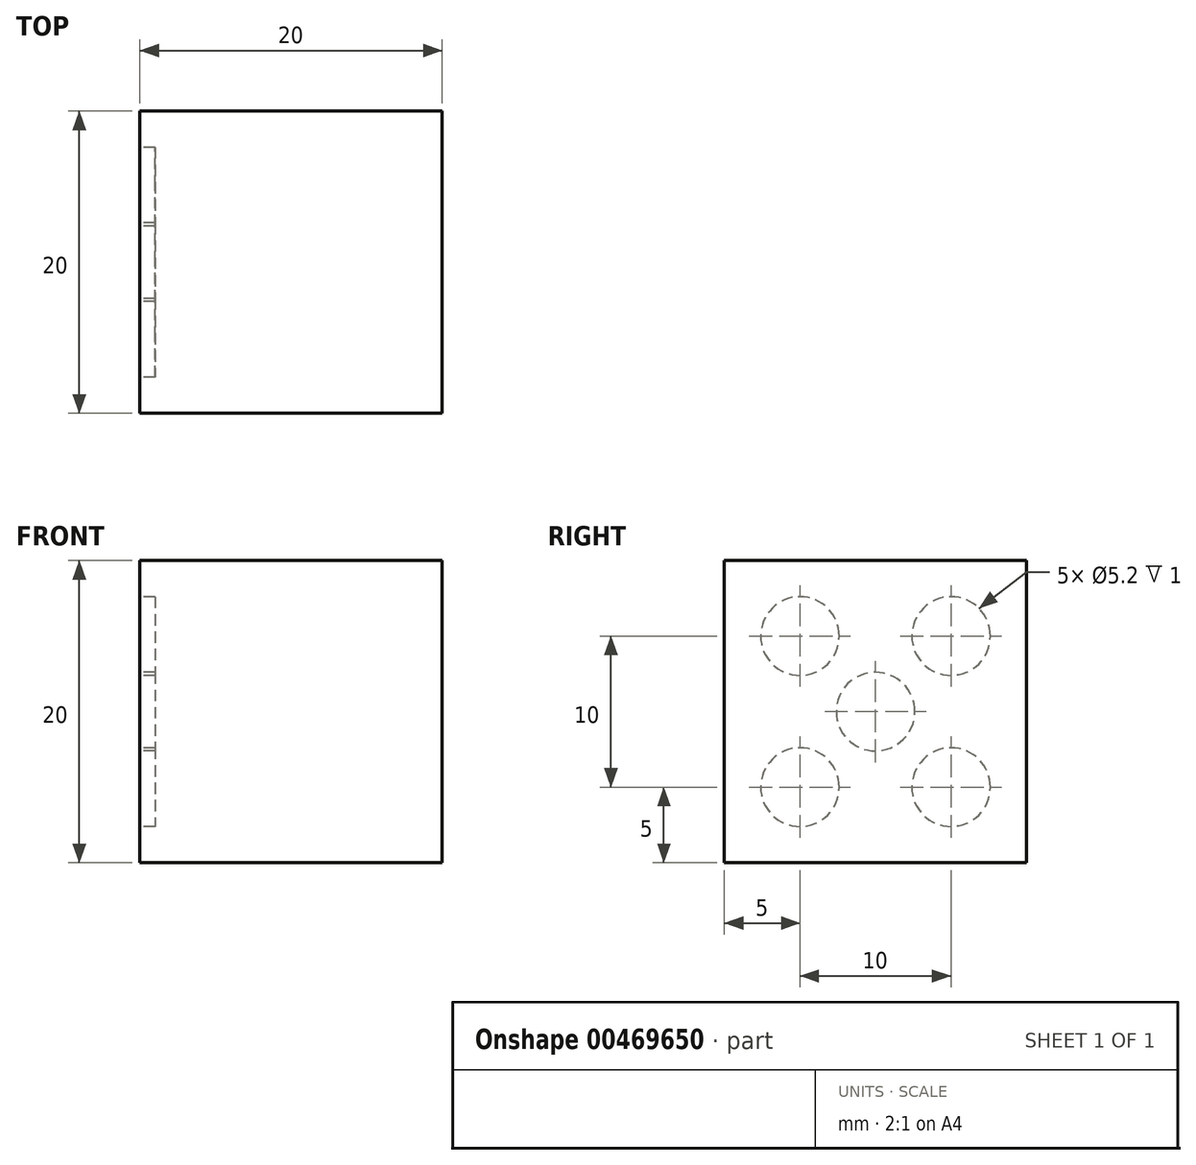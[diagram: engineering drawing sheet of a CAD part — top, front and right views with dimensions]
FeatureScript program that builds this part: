
annotation { "Feature Type Name" : "Feature", "Feature Type Description" : "" }
export const myFeature = defineFeature(function(context is Context, id is Id, definition is map)
    precondition{}
    {
        {
            var Q0;
            Q0=qCreatedBy(makeId("Front.planeOp"),FACE);
            var sketch = newSketch(context, id + "F0", { "sketchPlane" : qUnion([Q0])});
            skLineSegment(sketch, "E0.bottom", {"start": v(0, 0) * mm, "end": v(20, 0) * mm});
            skLineSegment(sketch, "E0.top", {"start": v(0, 20) * mm, "end": v(20, 20) * mm});
            skLineSegment(sketch, "E0.left", {"start": v(0, 0) * mm, "end": v(0, 20) * mm});
            skLineSegment(sketch, "E0.right", {"start": v(20, 0) * mm, "end": v(20, 20) * mm});
            skSolve(sketch);
        }
        {
            var Q0;
            Q0 = qSketchRegion(id + "F0", true);
            extrude(context, id + "F1", {"entities" : qUnion([Q0]), "depth" : 20 * mm});
        }
        {
            var Q0;
            Q0=makeQuery(id+"F1.opExtrude","SWEPT_FACE",FACE,{"disambiguationData":[OSD([sQuery(id+"F0.wireOp",EDGE,"E0.left")])]});
            var sketch = newSketch(context, id + "F2", { "sketchPlane" : qUnion([Q0])});
            skLineSegment(sketch, "E1", {"start": v(0, 20) * mm, "end": v(20, 0) * mm, "construction": true});
            skLineSegment(sketch, "E2", {"start": v(20, 0) * mm, "end": v(20, 20) * mm, "construction": true});
            skLineSegment(sketch, "E3", {"start": v(20, 20) * mm, "end": v(0, 0) * mm, "construction": true});
            skLineSegment(sketch, "E4", {"start": v(0, 0) * mm, "end": v(0, 10) * mm, "construction": true});
            skLineSegment(sketch, "E5", {"start": v(0, 10) * mm, "end": v(20, 10) * mm, "construction": true});
            skLineSegment(sketch, "E6", {"start": v(20, 10) * mm, "end": v(20, 20) * mm, "construction": true});
            skLineSegment(sketch, "E7", {"start": v(10, 20) * mm, "end": v(10, 0) * mm, "construction": true});
            skCircle(sketch, "E8", {"center": v(10, 10) * mm, "radius": 2.6 * mm});
            skCircle(sketch, "E9", {"center": v(5, 15) * mm, "radius": 2.6 * mm});
            skCircle(sketch, "E10.MirrorC", {"center": v(15, 15) * mm, "radius": 2.6 * mm});
            skCircle(sketch, "E11.MirrorC", {"center": v(5, 5) * mm, "radius": 2.6 * mm});
            skCircle(sketch, "E12.MirrorC", {"center": v(15, 5) * mm, "radius": 2.6 * mm});
            skSolve(sketch);
        }
        {
            var Q0;
            Q0 = qSketchRegion(id + "F2", true);
            extrude(context, id + "F3", {"entities" : qUnion([Q0]), "operationType" : NewBodyOperationType.REMOVE, "oppositeDirection" : true, "depth" : 1 * mm});
        }
    });
